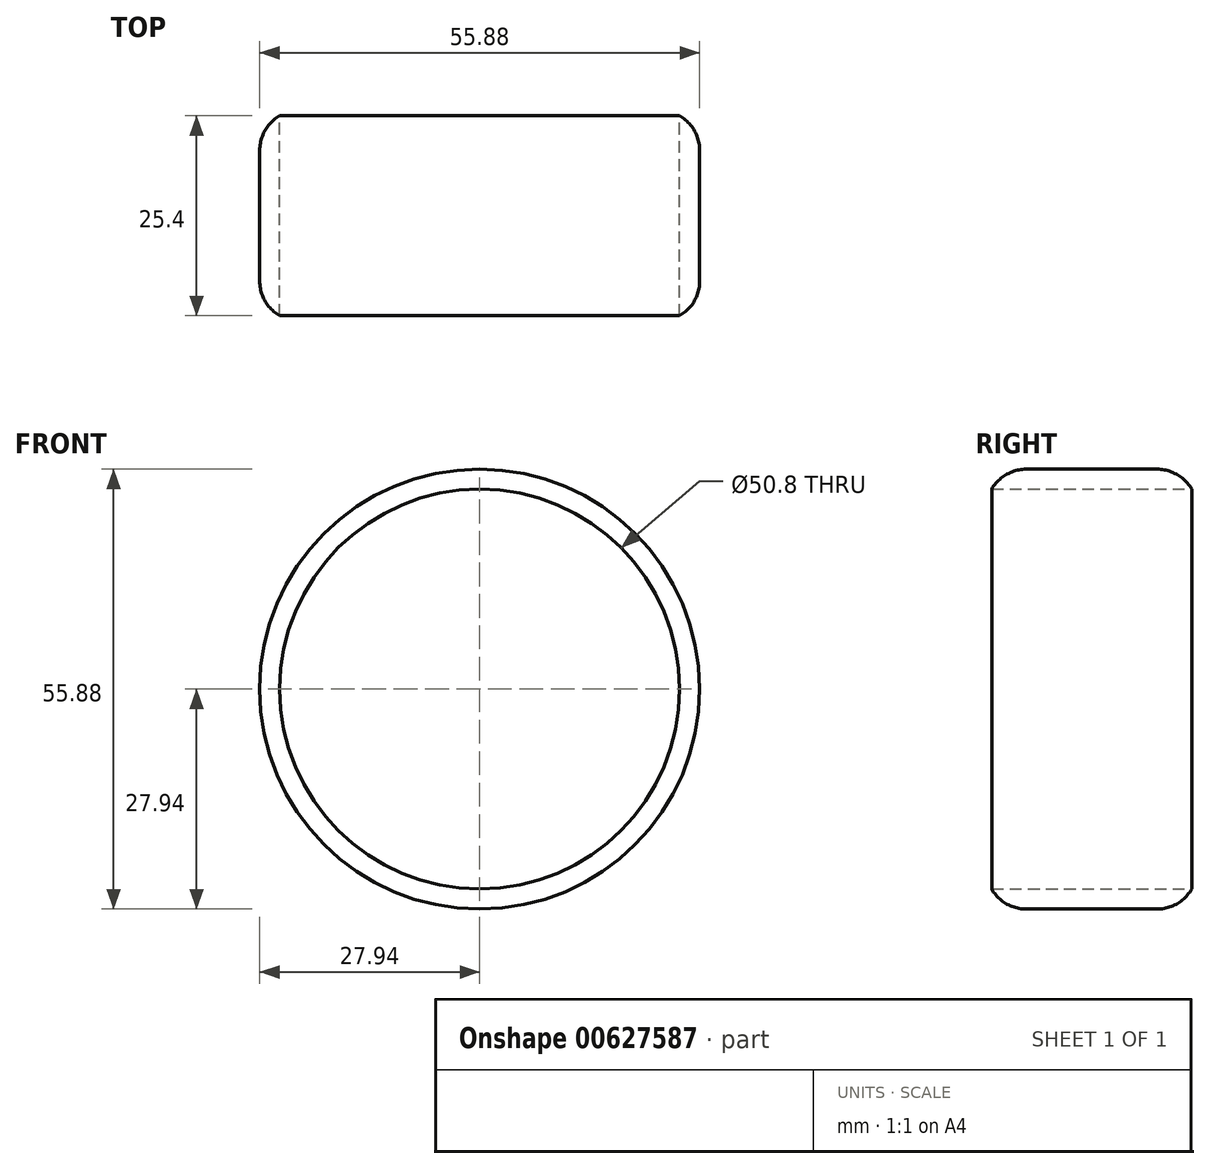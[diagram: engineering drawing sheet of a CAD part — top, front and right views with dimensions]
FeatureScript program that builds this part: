
annotation { "Feature Type Name" : "Feature", "Feature Type Description" : "" }
export const myFeature = defineFeature(function(context is Context, id is Id, definition is map)
    precondition{}
    {
        {
            var Q0;
            Q0=qCreatedBy(makeId("Front.planeOp"),FACE);
            var sketch = newSketch(context, id + "F0", { "sketchPlane" : qUnion([Q0])});
            skCircle(sketch, "E0", {"center": v(0, 0) * mm, "radius": 27.94 * mm});
            skCircle(sketch, "E1", {"center": v(0, 0) * mm, "radius": 25.4 * mm});
            skSolve(sketch);
        }
        {
            var Q0;
            Q0 = qSketchRegion(id + "F0", true);
            extrude(context, id + "F1", {"entities" : qUnion([Q0]), "depth" : 25.4 * mm, "offsetDistance" : 25.4 * mm});
        }
        {
            var Q0;
            Q0=makeQuery(id+"F1.opExtrude","CAP_EDGE",EDGE,{"disambiguationData":[OSD([sQuery(id+"F0.wireOp",EDGE,"E0")])],"isStart":true});
            var Q1;
            Q1=makeQuery(id+"F1.opExtrude","CAP_EDGE",EDGE,{"disambiguationData":[OSD([sQuery(id+"F0.wireOp",EDGE,"E0")])],"isStart":false});
            fillet(context, id + "F2", {"entities" : qUnion([Q0, Q1]), "radius" : 5.08 * mm, "tangentPropagation" : true, "allowEdgeOverflow" : false});
        }
    });
